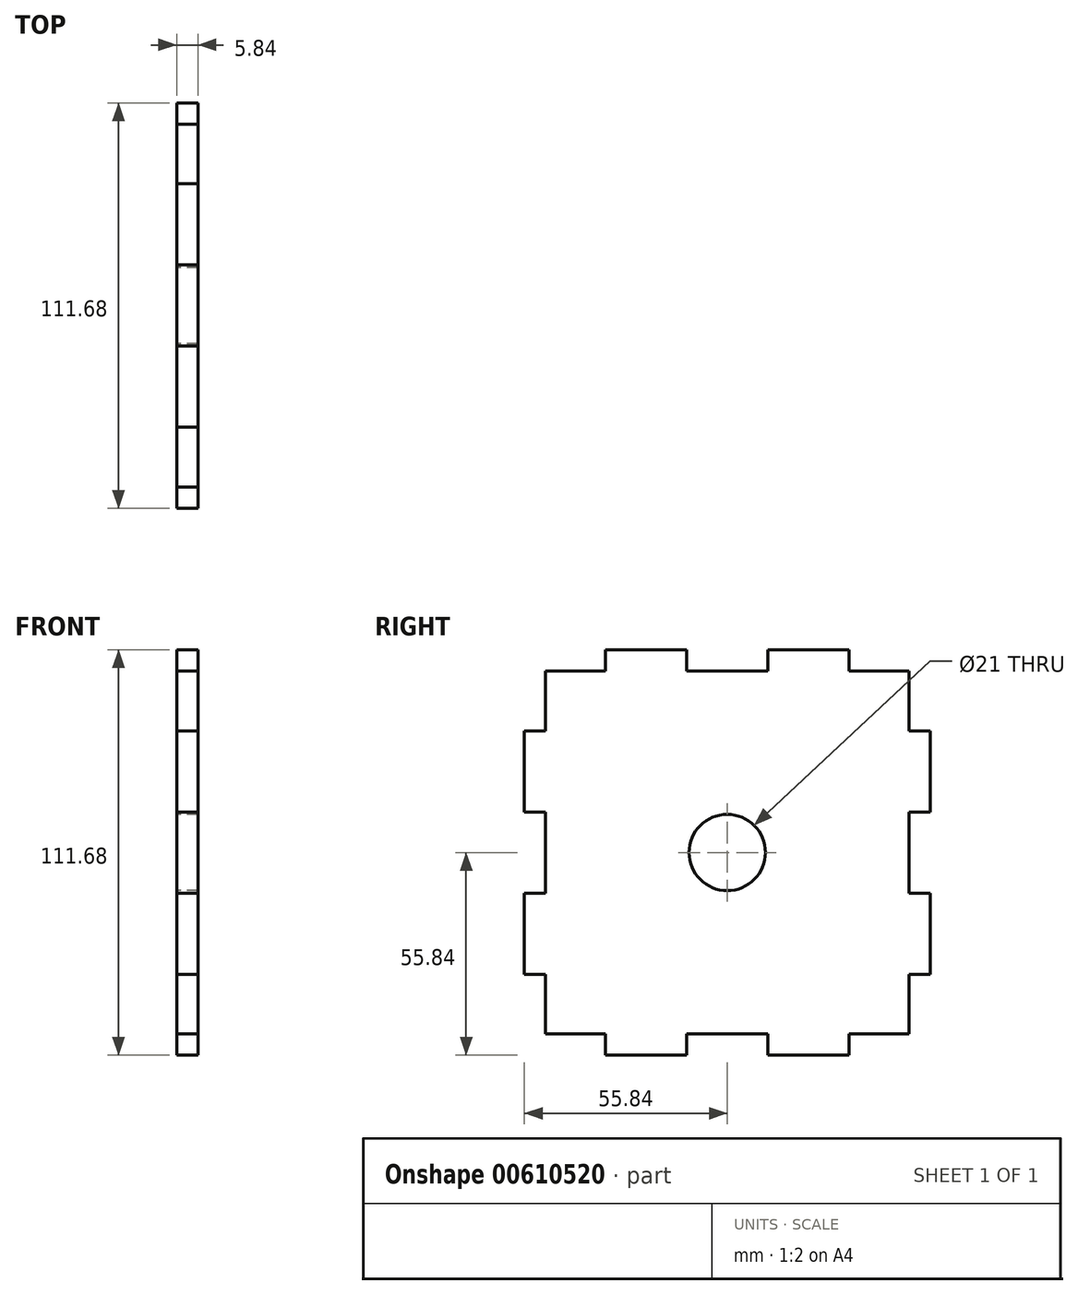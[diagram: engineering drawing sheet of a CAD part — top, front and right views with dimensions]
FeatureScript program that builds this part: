
annotation { "Feature Type Name" : "Feature", "Feature Type Description" : "" }
export const myFeature = defineFeature(function(context is Context, id is Id, definition is map)
    precondition{}
    {
        {
            var Q0;
            Q0=qCreatedBy(makeId("Right.planeOp"),FACE);
            var sketch = newSketch(context, id + "F0", { "sketchPlane" : qUnion([Q0])});
            skLineSegment(sketch, "E0.bottom", {"start": v(-50, 50) * mm, "end": v(50, 50) * mm});
            skLineSegment(sketch, "E0.top", {"start": v(-50, -50) * mm, "end": v(50, -50) * mm});
            skLineSegment(sketch, "E0.left", {"start": v(-50, 50) * mm, "end": v(-50, -50) * mm});
            skLineSegment(sketch, "E0.right", {"start": v(50, 50) * mm, "end": v(50, -50) * mm});
            skPoint(sketch, "E1.middle", {"position": v(0, 0) * mm});
            skLineSegment(sketch, "E2", {"start": v(-33.5, 50) * mm, "end": v(-33.5, 55.84) * mm});
            skLineSegment(sketch, "E3", {"start": v(-11.17, 50) * mm, "end": v(-11.17, 55.84) * mm});
            skPoint(sketch, "E3.endSnap0", {"position": v(0, 55.84) * mm});
            skLineSegment(sketch, "E4", {"start": v(11.17, 50) * mm, "end": v(11.17, 55.84) * mm});
            skLineSegment(sketch, "E5", {"start": v(33.5, 50) * mm, "end": v(33.5, 55.84) * mm});
            skLineSegment(sketch, "E6", {"start": v(-50, 33.5) * mm, "end": v(-55.84, 33.5) * mm});
            skLineSegment(sketch, "E7", {"start": v(-50, 11.17) * mm, "end": v(-55.84, 11.17) * mm});
            skLineSegment(sketch, "E8", {"start": v(-50, -11.17) * mm, "end": v(-55.84, -11.17) * mm});
            skLineSegment(sketch, "E9", {"start": v(-50, -33.5) * mm, "end": v(-55.84, -33.5) * mm});
            skLineSegment(sketch, "E10", {"start": v(-33.5, -50) * mm, "end": v(-33.5, -55.84) * mm});
            skLineSegment(sketch, "E11", {"start": v(-11.17, -50) * mm, "end": v(-11.17, -55.84) * mm});
            skLineSegment(sketch, "E12", {"start": v(11.17, -50) * mm, "end": v(11.17, -55.84) * mm});
            skLineSegment(sketch, "E13", {"start": v(33.5, -50) * mm, "end": v(33.5, -55.84) * mm});
            skLineSegment(sketch, "E14", {"start": v(50, -33.5) * mm, "end": v(55.84, -33.5) * mm});
            skLineSegment(sketch, "E15", {"start": v(50, -11.17) * mm, "end": v(55.84, -11.17) * mm});
            skLineSegment(sketch, "E16", {"start": v(50, 11.17) * mm, "end": v(55.84, 11.17) * mm});
            skLineSegment(sketch, "E17", {"start": v(50, 33.5) * mm, "end": v(55.84, 33.5) * mm});
            skLineSegment(sketch, "E18", {"start": v(55.84, 33.5) * mm, "end": v(55.84, 11.17) * mm});
            skLineSegment(sketch, "E19", {"start": v(55.84, -11.17) * mm, "end": v(55.84, -33.5) * mm});
            skLineSegment(sketch, "E20", {"start": v(11.17, -55.84) * mm, "end": v(33.5, -55.84) * mm});
            skLineSegment(sketch, "E21", {"start": v(-33.5, -55.84) * mm, "end": v(-11.17, -55.84) * mm});
            skLineSegment(sketch, "E22", {"start": v(-55.84, -33.5) * mm, "end": v(-55.84, -11.17) * mm});
            skLineSegment(sketch, "E23", {"start": v(-55.84, 33.5) * mm, "end": v(-55.84, 11.17) * mm});
            skLineSegment(sketch, "E24", {"start": v(-33.5, 55.84) * mm, "end": v(-11.17, 55.84) * mm});
            skLineSegment(sketch, "E25", {"start": v(11.17, 55.84) * mm, "end": v(33.5, 55.84) * mm});
            skPoint(sketch, "E1.left.start.orphan", {"position": v(-55.84, 55.84) * mm});
            skPoint(sketch, "E1.top.start.orphan", {"position": v(-55.84, -55.84) * mm});
            skPoint(sketch, "E26.trimOffspring.end.orphan", {"position": v(55.84, -55.84) * mm});
            skPoint(sketch, "E27.trimOffspring.end.orphan", {"position": v(55.84, 55.84) * mm});
            skCircle(sketch, "E28", {"center": v(0, 0) * mm, "radius": 10.5 * mm});
            skSolve(sketch);
        }
        {
            var Q0;
            Q0=qSketchRegion(id+"F0",true);
            extrude(context, id + "F1", {"entities" : qUnion([Q0]), "depth" : 5.84 * mm, "offsetDistance" : 25 * mm});
        }
    });
